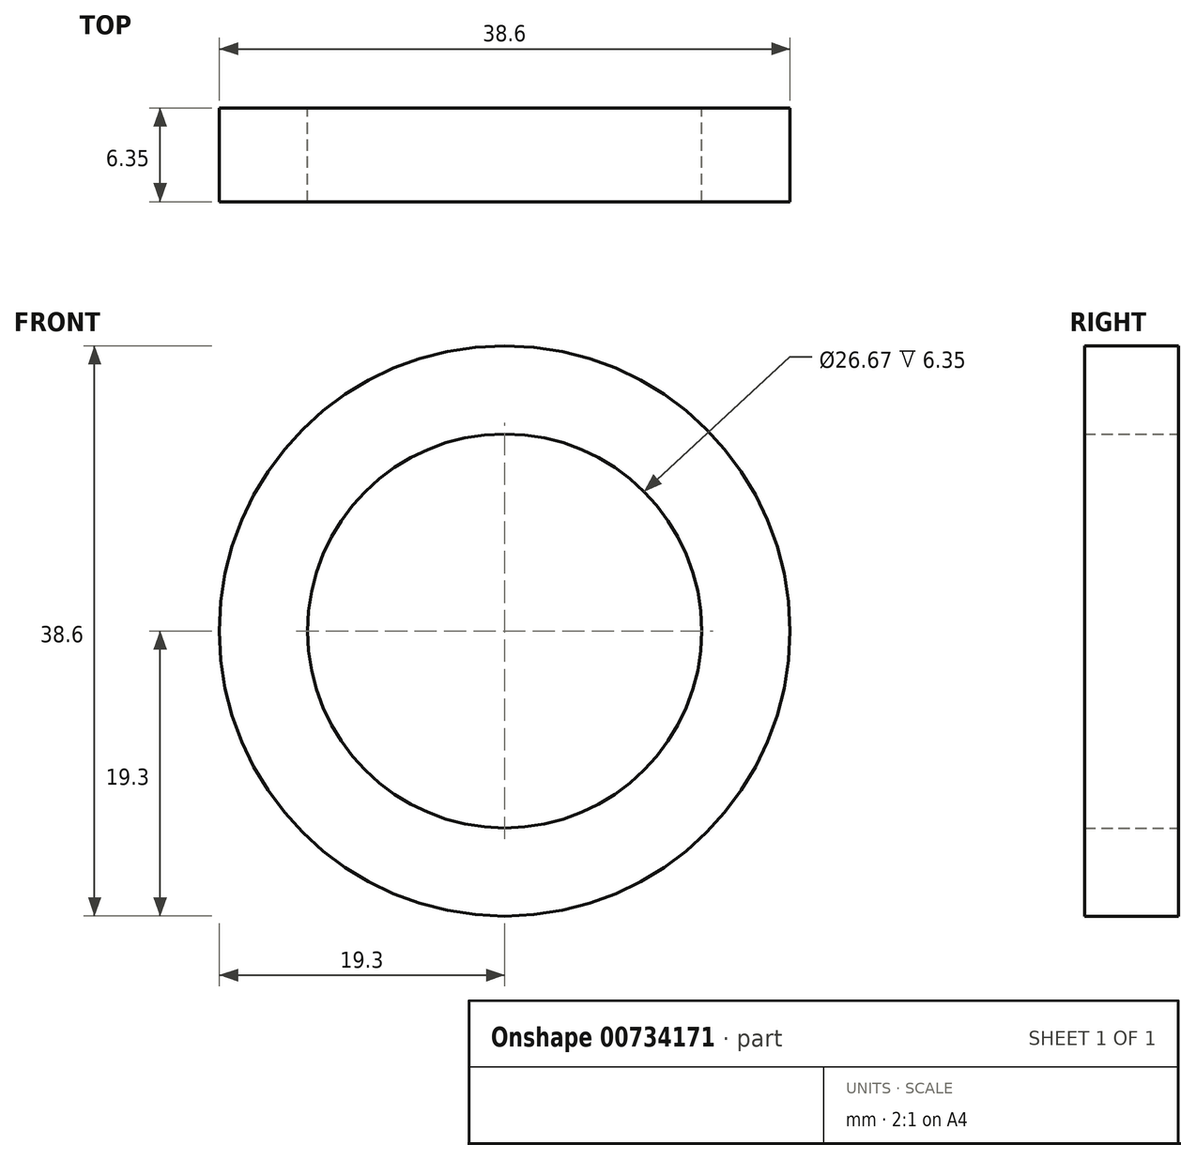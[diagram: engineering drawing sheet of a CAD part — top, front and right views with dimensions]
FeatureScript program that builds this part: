
annotation { "Feature Type Name" : "Feature", "Feature Type Description" : "" }
export const myFeature = defineFeature(function(context is Context, id is Id, definition is map)
    precondition{}
    {
        {
            var Q0;
            Q0=qCreatedBy(makeId("Front.planeOp"),FACE);
            var sketch = newSketch(context, id + "F0", { "sketchPlane" : qUnion([Q0])});
            skCircle(sketch, "E0", {"center": v(0, 0) * mm, "radius": 13.34 * mm});
            skCircle(sketch, "E1", {"center": v(0, 0) * mm, "radius": 19.3 * mm});
            skSolve(sketch);
        }
        {
            var Q0;
            Q0 = qSketchRegion(id + "F0", true);
            extrude(context, id + "F1", {"entities" : qUnion([Q0]), "depth" : 6.35 * mm, "offsetDistance" : 25.4 * mm});
        }
    });
